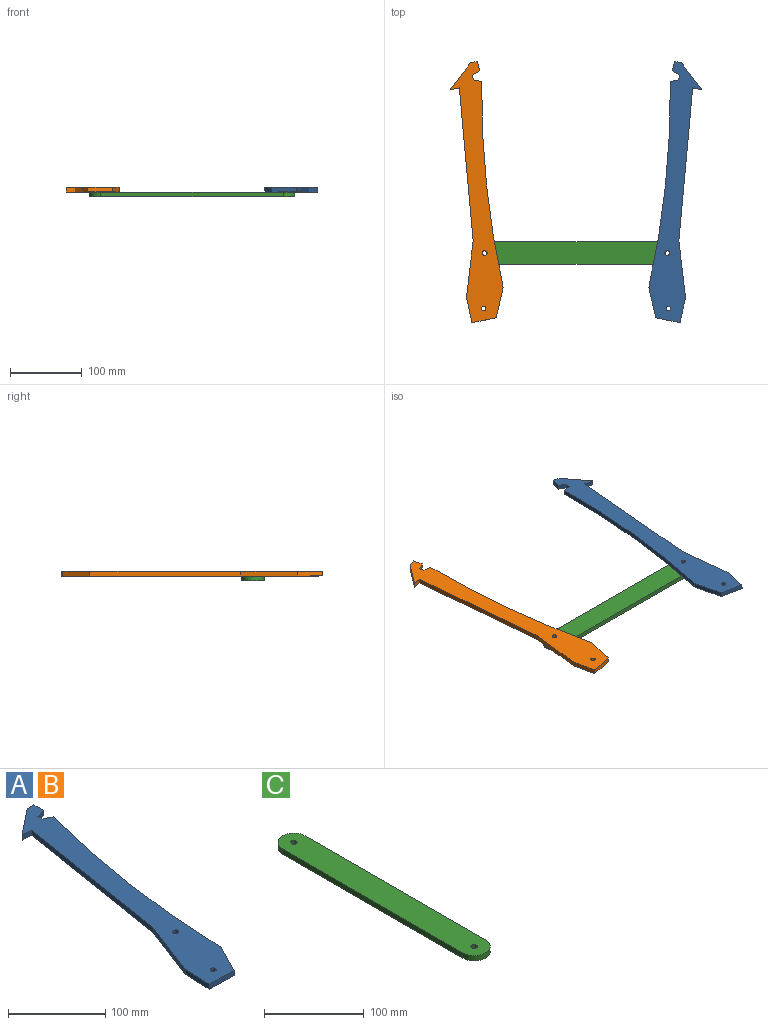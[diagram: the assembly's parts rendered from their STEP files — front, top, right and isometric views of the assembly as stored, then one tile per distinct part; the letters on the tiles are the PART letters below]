
ASSEMBLY  parts=3 mates=2
PART A: 17 faces, bbox 98.2x353.7x6.4 mm
  f0: plane 11.49x6.35mm, normal (0.28,-0.96,0), area 75.9mm2, adj f1,f13,f15,f16
  f1: plane 14.04x6.35mm, normal (1,0,0), area 89.1mm2, adj f0,f2,f15,f16
  f2: plane 9.61x6.35mm, normal (0,1,0), area 61mm2, adj f1,f3,f15,f16
  f3: plane 36.9x29.23mm, normal (-0.62,0.78,0), area 298.9mm2, adj f2,f4,f15,f16
  f4: plane 12.99x6.35mm, normal (-0.05,-1,0), area 82.6mm2, adj f3,f5,f15,f16
  f5: plane 211.84x34.4mm, normal (-0.99,0.16,0), area 1362.8mm2, adj f4,f6,f15,f16
  f6: plane 74.81x28.8mm, normal (-0.93,0.36,0), area 509.1mm2, adj f5,f7,f15,f16
  f7: plane 35.84x6.35mm, normal (-1,0.04,0), area 227.8mm2, adj f6,f8,f15,f16
  f8: plane 34.8x6.35mm, normal (-0.04,-1,0), area 221.1mm2, adj f7,f9,f15,f16
  f9: plane 38.55x19.92mm, normal (0.89,-0.46,0), area 275.5mm2, adj f8,f10,f15,f16
  f10: cylinder r=1262.83mm len=286.25mm, axis (0,0,-1), area 1841.6mm2, adj f9,f11,f15,f16
  f11: plane 10.79x6.35mm, normal (0.42,0.91,0), area 75.3mm2, adj f10,f13,f15,f16
  f12: cylinder r=3.13mm len=6.35mm, axis (0,0,-1), area 124.8mm2, adj f15,f16
  f13: plane 6.7x6.35mm, normal (1,-0.05,0), area 42.6mm2, adj f0,f11,f15,f16
  f14: cylinder r=3.17mm len=6.35mm, axis (0,0,-1), area 126.5mm2, adj f15,f16
  f15: plane 353.74x98.16mm, normal (0,0,1), area 11136.9mm2, adj f0,f1,f2,f3,f4,f5,f6,f7
  f16: plane 353.74x98.16mm, normal (0,0,-1), area 11136.9mm2, adj f0,f1,f2,f3,f4,f5,f6,f7
PART B: same geometry as A
PART C: 8 faces, bbox 31.8x286.8x6.4 mm
  f0: cylinder r=15.88mm len=31.75mm, axis (0,0,-1), area 316.7mm2, adj f1,f4,f6,f7
  f1: plane 255x6.35mm, normal (-1,0,0), area 1619.2mm2, adj f0,f2,f6,f7
  f2: cylinder r=15.88mm len=31.75mm, axis (0,0,-1), area 316.7mm2, adj f1,f4,f6,f7
  f3: cylinder r=3.17mm len=6.35mm, axis (0,0,-1), area 126.7mm2, adj f6,f7
  f4: plane 255x6.35mm, normal (1,0,0), area 1619.2mm2, adj f0,f2,f6,f7
  f5: cylinder r=3.17mm len=6.35mm, axis (0,0,-1), area 126.7mm2, adj f6,f7
  f6: plane 286.75x31.75mm, normal (0,0,1), area 8824.6mm2, adj f0,f1,f2,f3,f4,f5
  f7: plane 286.75x31.75mm, normal (0,0,-1), area 8824.6mm2, adj f0,f1,f2,f3,f4,f5
PLACE A rot(axis=(0.13,0.99,0),180deg) t=(132.82,-46.88,12.7)mm
PLACE B rot(axis=(0,0,1),14.4deg) t=(-132.82,-46.88,6.35)mm
PLACE C rot(axis=(0,0,-1),90deg) t=(0,0,0)mm
MATE revolute C.f5 <-> B.f14  axis (0,0,1) through (-127.5,0,6.35)mm
MATE revolute C.f0 <-> A.f14  axis (0,0,1) through (127.5,0,6.35)mm
